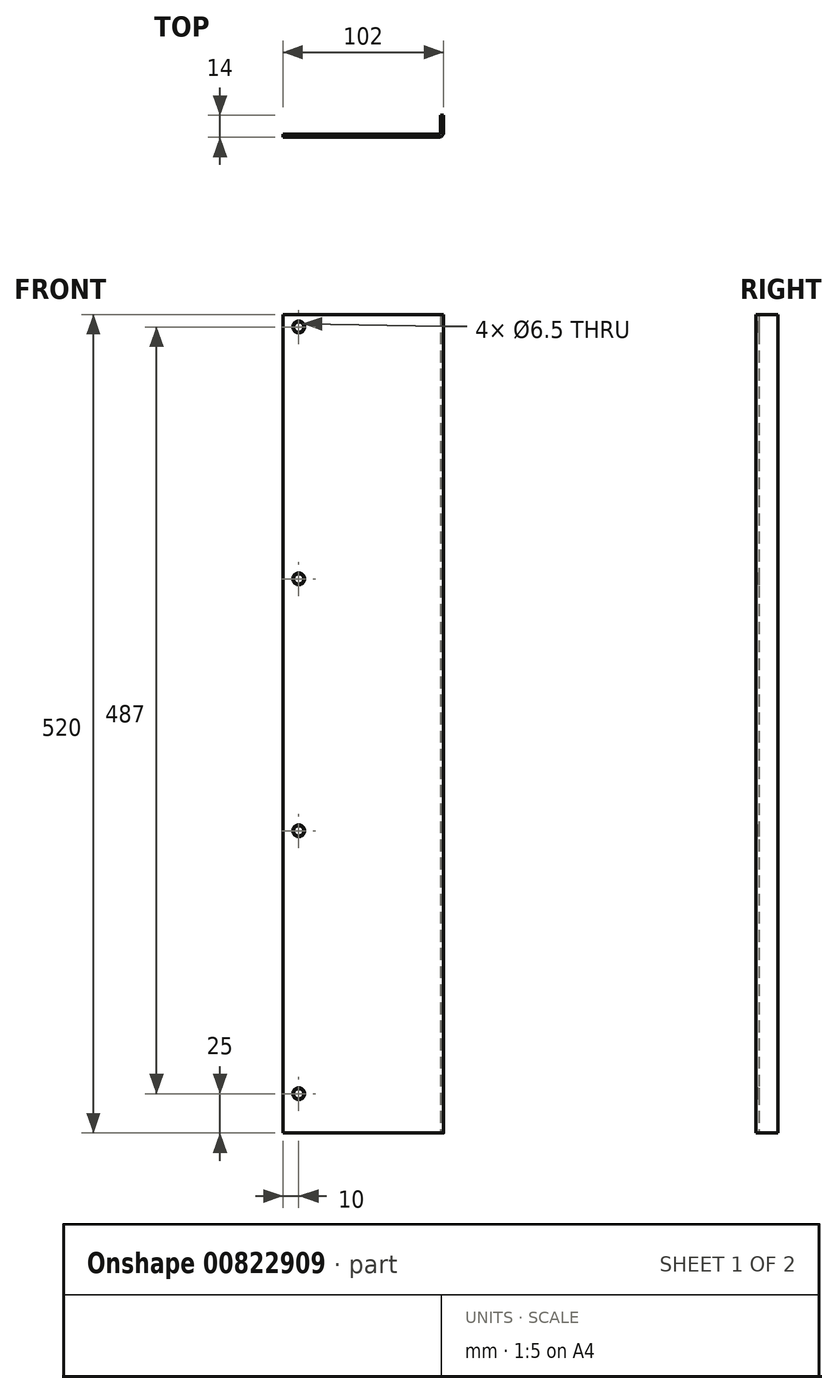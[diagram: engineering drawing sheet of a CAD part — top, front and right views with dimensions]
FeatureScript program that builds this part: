
annotation { "Feature Type Name" : "Feature", "Feature Type Description" : "" }
export const myFeature = defineFeature(function(context is Context, id is Id, definition is map)
    precondition{}
    {
        {
            var Q0;
            Q0=qCreatedBy(makeId("Top.planeOp"),FACE);
            var sketch = newSketch(context, id + "F0", { "sketchPlane" : qUnion([Q0])});
            skLineSegment(sketch, "E0", {"start": v(0, 1) * mm, "end": v(0, 12) * mm});
            skLineSegment(sketch, "E1", {"start": v(0, 12) * mm, "end": v(2, 12) * mm});
            skLineSegment(sketch, "E2", {"start": v(2, 12) * mm, "end": v(2, 1) * mm});
            skLineSegment(sketch, "E3", {"start": v(-1, -2) * mm, "end": v(-100, -2) * mm});
            skLineSegment(sketch, "E4", {"start": v(-100, -2) * mm, "end": v(-100, 0) * mm});
            skLineSegment(sketch, "E5", {"start": v(-100, 0) * mm, "end": v(-1, 0) * mm});
            skPoint(sketch, "E6.visualSharp", {"position": v(0, 0) * mm});
            skArc(sketch, "E6.filletArc", {"start": v(-1, 0) * mm, "mid": v(-0.3, 0.3) * mm, "end": v(0, 1) * mm});
            skPoint(sketch, "E7.visualSharp", {"position": v(2, -2) * mm});
            skArc(sketch, "E7.filletArc", {"start": v(-1, -2) * mm, "mid": v(1.12, -1.12) * mm, "end": v(2, 1) * mm});
            skSolve(sketch);
        }
        {
            var Q0;
            Q0 = qSketchRegion(id + "F0", true);
            extrude(context, id + "F1", {"entities" : qUnion([Q0]), "endBound" : BoundingType.SYMMETRIC, "depth" : 520 * mm, "offsetDistance" : 25 * mm});
        }
        {
            var Q0;
            Q0=makeQuery(id+"F1.opExtrude","SWEPT_FACE",FACE,{"disambiguationData":[OSD([sQuery(id+"F0.wireOp",EDGE,"E3")])]});
            var sketch = newSketch(context, id + "F2", { "sketchPlane" : qUnion([Q0])});
            skLineSegment(sketch, "E8.0.0", {"start": v(-100, -260) * mm, "end": v(-1, -260) * mm, "construction": true});
            skLineSegment(sketch, "E8.0.1", {"start": v(-1, -260) * mm, "end": v(-1, 260) * mm, "construction": true});
            skLineSegment(sketch, "E8.0.2", {"start": v(-1, 260) * mm, "end": v(-100, 260) * mm, "construction": true});
            skLineSegment(sketch, "E8.0.3", {"start": v(-100, 260) * mm, "end": v(-100, -260) * mm, "construction": true});
            skLineSegment(sketch, "E9", {"start": v(-90, 260) * mm, "end": v(-90, -260) * mm, "construction": true});
            skCircle(sketch, "E10", {"center": v(-90, 252) * mm, "radius": 3.25 * mm});
            skCircle(sketch, "E11", {"center": v(-90, -235) * mm, "radius": 3.25 * mm});
            skCircle(sketch, "E12.0.1.0", {"center": v(-90, 92) * mm, "radius": 3.25 * mm});
            skCircle(sketch, "E12.0.2.0", {"center": v(-90, -68) * mm, "radius": 3.25 * mm});
            skLineSegment(sketch, "E12.direction1", {"start": v(-90, 252) * mm, "end": v(-49.84, 252) * mm, "construction": true});
            skLineSegment(sketch, "E12.direction2", {"start": v(-90, 252) * mm, "end": v(-90, 92) * mm, "construction": true});
            skSolve(sketch);
        }
        {
            var Q0;
            Q0 = qSketchRegion(id + "F2", true);
            extrude(context, id + "F3", {"entities" : qUnion([Q0]), "operationType" : NewBodyOperationType.REMOVE, "oppositeDirection" : true, "depth" : 25 * mm, "offsetDistance" : 25 * mm});
        }
        {
            var Q0;
            Q0=makeQuery(id+"F3.boolean.opBoolean","COPY",FACE,{"derivedFrom":makeQuery(id+"F3.opExtrude","SWEPT_FACE",FACE,{"disambiguationData":[OSD([sQuery(id+"F2.wireOp",EDGE,"E10")])]})});
            var Q1;
            Q1=makeQuery(id+"F3.boolean.opBoolean","COPY",FACE,{"derivedFrom":makeQuery(id+"F3.opExtrude","SWEPT_FACE",FACE,{"disambiguationData":[OSD([sQuery(id+"F2.wireOp",EDGE,"E12.0.1.0")])]})});
            var Q2;
            Q2=makeQuery(id+"F3.boolean.opBoolean","COPY",FACE,{"derivedFrom":makeQuery(id+"F3.opExtrude","SWEPT_FACE",FACE,{"disambiguationData":[OSD([sQuery(id+"F2.wireOp",EDGE,"E12.0.2.0")])]})});
            var Q3;
            Q3=makeQuery(id+"F3.boolean.opBoolean","COPY",FACE,{"derivedFrom":makeQuery(id+"F3.opExtrude","SWEPT_FACE",FACE,{"disambiguationData":[OSD([sQuery(id+"F2.wireOp",EDGE,"E11")])]})});
            chamfer(context, id + "F4", {"entities" : qUnion([Q0, Q1, Q2, Q3]), "width" : .5 * mm, "tangentPropagation" : true});
        }
    });
